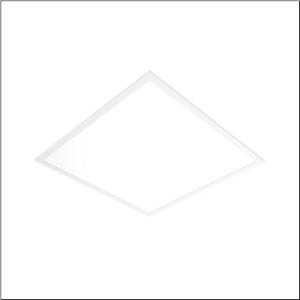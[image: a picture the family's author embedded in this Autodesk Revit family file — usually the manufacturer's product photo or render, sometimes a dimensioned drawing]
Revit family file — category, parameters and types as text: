
# Revit family: apollon_r__41_51mh12w72443m_8ad7
name_source: partatom
category: Lighting Fixtures
units: mm (PartAtom-declared; Revit-internal decimal feet)

## family parameters
Cut with Voids When Loaded = No
Host = Face
Light Source = No
Part Type = Normal
Room Calculation Point = No
Round Connector Dimension = Use Diameter
Shared = No

## types (1)
- Apollon® 41 (1 x LED, 3700 lm, 28.5 W, 4000K)
    Apparent Load = 29 VA
    CIE Flux Codes = 61 87 97 100 100
    Color Rendering = 80
    Color Temperature = 4000K
    Default Elevation = 1800 mm
    Description = Apollon® 41, office luminaire, primary optical cover: prismatic diffuser, of PS, light emission: direct distribution, primary light characteristic: symmetric, installation type: lay-in mounting, LED, rated luminous flux: 3.700lm, luminous efficacy: 130lm/W, light colour: 840, colour temperature: 4000K, with terminal, 3-pole, mains connection: 220..240V, AC, 50/60Hz, housing, of aluminium section, traffic white (RAL 9016), module: M600, length: 600mm, width: 600mm, height: 28mm, housing upper side, of sheet steel, protection rating (complete): IP20, protection rating (lamp compartment, on room side): IP40, insulation class (complete): insulation class II (safety insulation), certification: CE, ENEC, permissible operating ambient temperature: -25..+40°C, packaging unit: set of 6
    Height = 0 mm  [stored 0 ft]
    Lamp = 1 x LED
    Lamp Light Flux = 3700 lm
    Lamp Power = 28.5 W
    Lamp count = 1
    Length = 600 mm
    Luminous efficacy = 130 lm/W
    Manufacturer = Siteco
    ModVariant = No
    Model = 51MH12W72443M
    Mounting Place = Ceiling
    Mounting Type = Recessed
    Number of Poles = 1
    OnlyDefault = Yes
    Power Factor = 1
    Product Name = Apollon® 41
    Product group = office luminaire | ceiling recessed
    ProductGroupID = 401
    Protection Class = Protection class II
    Protection Degree = IP 20
    RLX_Detail_Level = 1
    RLX_Emergency_Light_Flux = 0 lm
    RLX_Emergency_Type = 0
    RLX_Emergency_Type_DB = No
    RlxData = <blob elided: 12197 chars, md5=15c36b1f>
    Socket = socket
    Standby Power = 0 W
    System Light Flux = 3700 lm
    System Power = 29 W
    Type Comments = Product without accessories
    Type Image = l_1291024.jpg
    URL = http://relux.com
    VarID = ---
    Voltage = 0 V
    Weight = 0.00 kg
    Width = 600 mm

note: [stored X ft] marks values corroborated as IEEE doubles in the binary element streams (Revit-internal decimal feet)

## geometry (parser evidence)
native form markers: Sweep x11
no freeform markers — native parametric forms only
